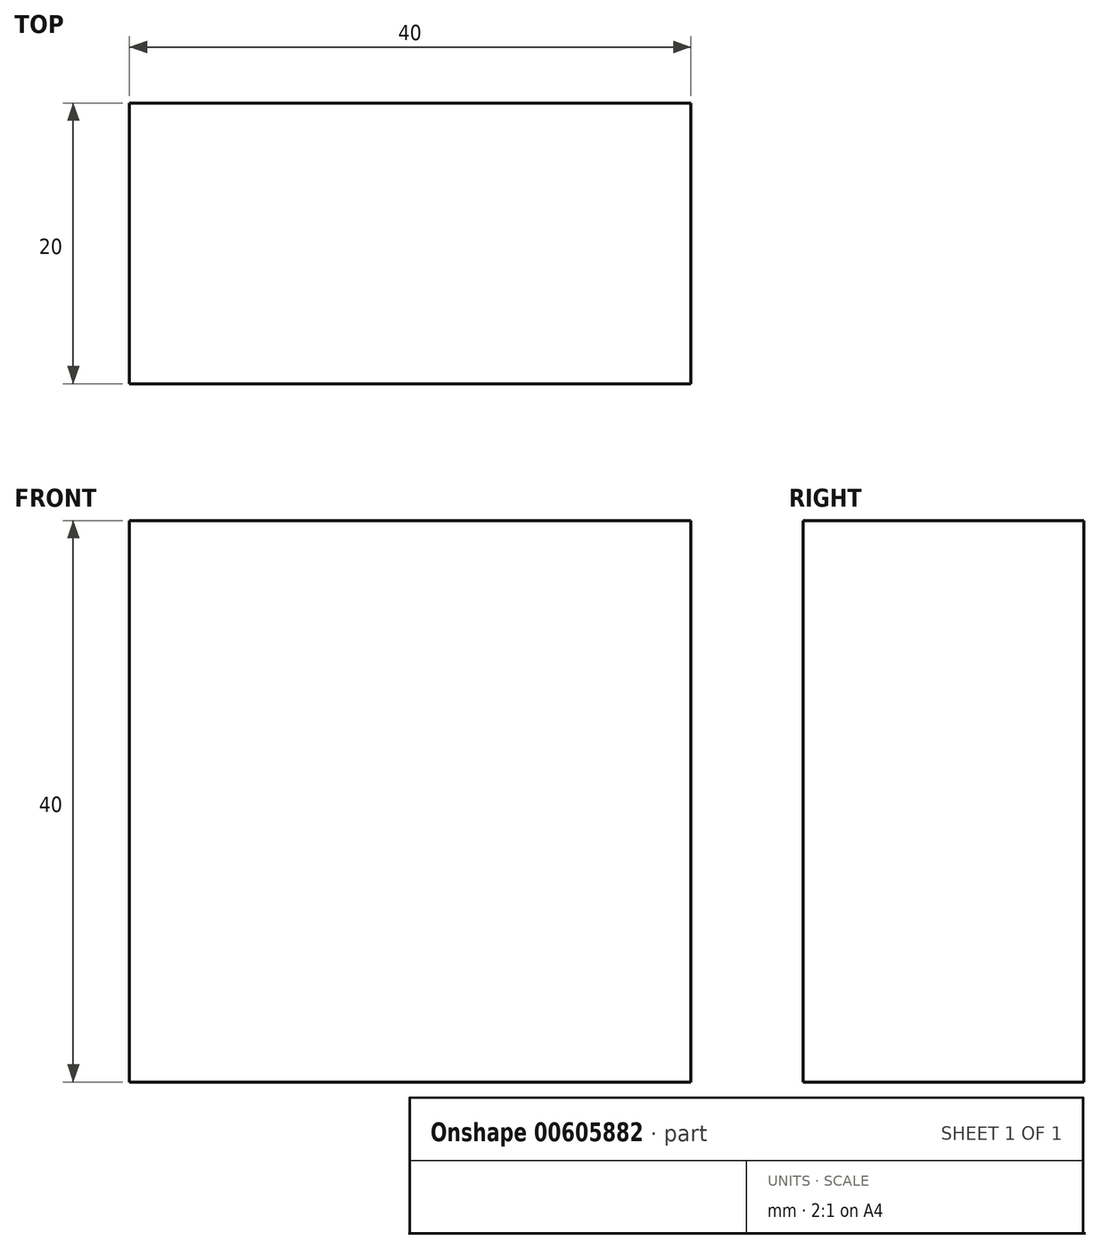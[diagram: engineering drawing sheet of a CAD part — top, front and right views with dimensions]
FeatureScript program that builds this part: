
annotation { "Feature Type Name" : "Feature", "Feature Type Description" : "" }
export const myFeature = defineFeature(function(context is Context, id is Id, definition is map)
    precondition{}
    {
        {
            var Q0;
            Q0=qCreatedBy(makeId("Front.planeOp"),FACE);
            var sketch = newSketch(context, id + "F0", { "sketchPlane" : qUnion([Q0])});
            skLineSegment(sketch, "E0", {"start": v(-30.65, 37.83) * mm, "end": v(9.35, 37.83) * mm});
            skLineSegment(sketch, "E1", {"start": v(9.35, 37.83) * mm, "end": v(9.35, -2.17) * mm});
            skLineSegment(sketch, "E2", {"start": v(9.35, -2.17) * mm, "end": v(-30.65, -2.17) * mm});
            skLineSegment(sketch, "E3", {"start": v(-30.65, -2.17) * mm, "end": v(-30.65, 37.83) * mm});
            skSolve(sketch);
        }
        {
            var Q0;
            Q0 = qSketchRegion(id + "F0", true);
            extrude(context, id + "F1", {"entities" : qUnion([Q0]), "depth" : 20 * mm, "offsetDistance" : 25 * mm});
        }
    });
